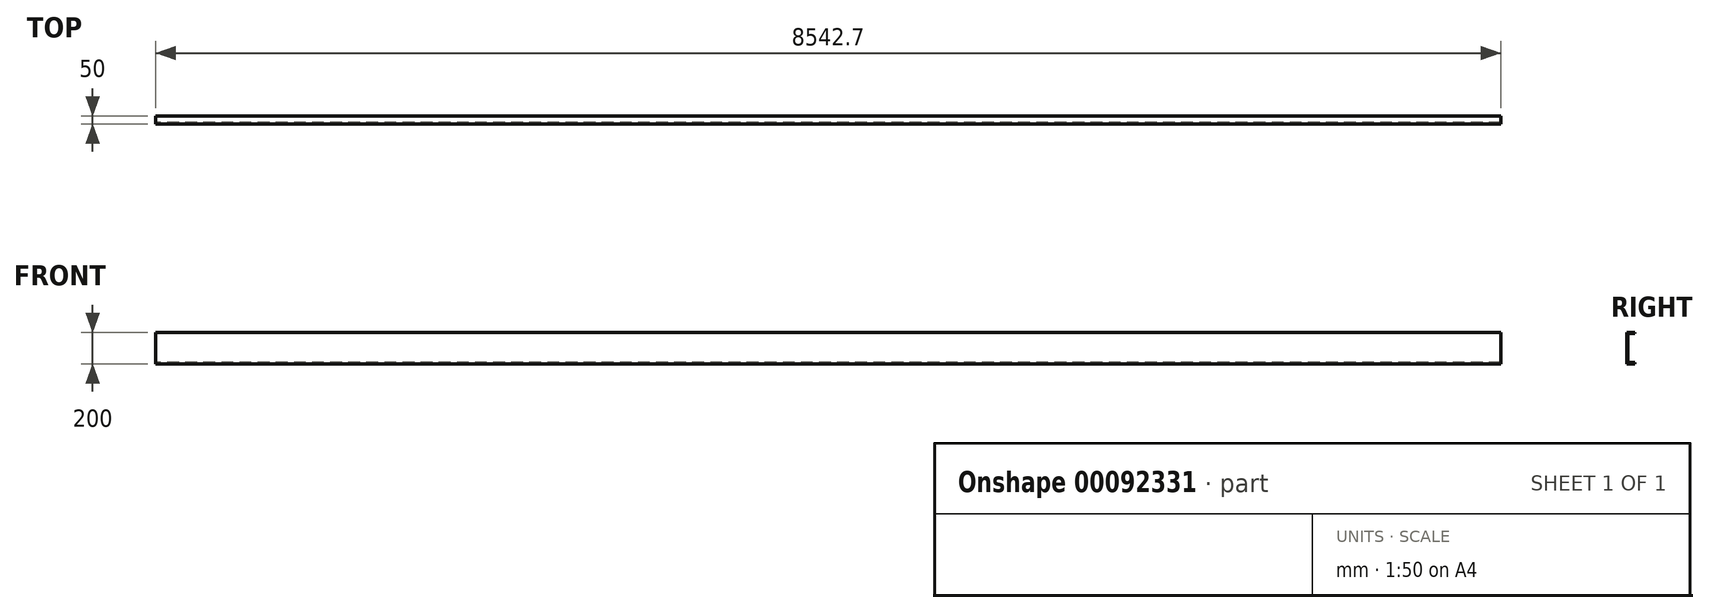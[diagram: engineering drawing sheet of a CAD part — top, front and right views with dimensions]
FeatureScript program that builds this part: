
annotation { "Feature Type Name" : "Feature", "Feature Type Description" : "" }
export const myFeature = defineFeature(function(context is Context, id is Id, definition is map)
    precondition{}
    {
        {
            var Q0;
            Q0=qCreatedBy(makeId("Right.planeOp"),FACE);
            var sketch = newSketch(context, id + "F0", { "sketchPlane" : qUnion([Q0])});
            skLineSegment(sketch, "E0", {"start": v(0, 0) * mm, "end": v(-50, 0) * mm});
            skLineSegment(sketch, "E1", {"start": v(-50, 0) * mm, "end": v(-50, 200) * mm});
            skLineSegment(sketch, "E2", {"start": v(-50, 200) * mm, "end": v(0, 200) * mm});
            skLineSegment(sketch, "E3", {"start": v(0, 200) * mm, "end": v(0, 192) * mm});
            skLineSegment(sketch, "E4", {"start": v(0, 192) * mm, "end": v(-42, 192) * mm});
            skLineSegment(sketch, "E5", {"start": v(-42, 192) * mm, "end": v(-42, 8) * mm});
            skLineSegment(sketch, "E6", {"start": v(-42, 8) * mm, "end": v(0, 8) * mm});
            skLineSegment(sketch, "E7", {"start": v(0, 8) * mm, "end": v(0, 0) * mm});
            skSolve(sketch);
        }
        {
            var Q0;
            Q0=qSketchRegion(id+"F0",true);
            extrude(context, id + "F1", {"entities" : qUnion([Q0]), "offsetDistance" : 25 * mm, "depth" : 8542.7 * mm});
        }
    });
